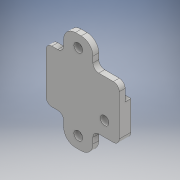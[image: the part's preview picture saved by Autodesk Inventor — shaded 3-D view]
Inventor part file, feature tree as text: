
AUTODESK INVENTOR PART (.ipt)
format: ipt  version: 2017 (Build 210142000, 142)  size: 181,248 bytes
history: native  units: mm
features: extrude x3, sketch x1, hole x1
ambient origin geometry x8: Origin, YZ Plane, XZ Plane, XY Plane, X Axis, Y Axis, Z Axis, Center Point
bodies: Solid1 (feature_tree)
feature tree (5):
  sketch  "Sketch1"  dims[d9=6.0mm d10=26.0mm d11=9.0mm d12=15.0mm d13=5.0mm d14=5.0mm d17=4.0mm d18=4.0mm d20=4.0mm d21=4.0mm d22=4.0mm d23=4.0mm d25=5.0mm d26=5.0mm d27=18.0mm d28=1.0mm d29=2.0mm d30=6.0mm d31=1.0mm d32=6.0mm d34=4.0mm d35=2.0mm d37=10.0mm d38=6.0mm d39=2.0mm d40=2.0mm d41=0.0mm d42=4.0mm d43=0.0mm d44=3.0mm d45=6.0mm d46=4.0mm d47=2.0mm d48=90.0deg d49=8.0mm d50=20.594885mm d54=3.0mm d55=5.0mm d56=0.0mm]
  extrude  "Extrusion1"  Depth=26.0mm
  extrude  "Extrusion2"  Depth=9.0mm
  hole  "Hole1"  [1 undecoded]
  extrude  "Extrusion4"  Depth=5.0mm
note: 1 required parameter value undecoded (feature->parameter linkage not recoverable at this tier; creation-order binding heuristic only, values carry confidence <= 0.55)
